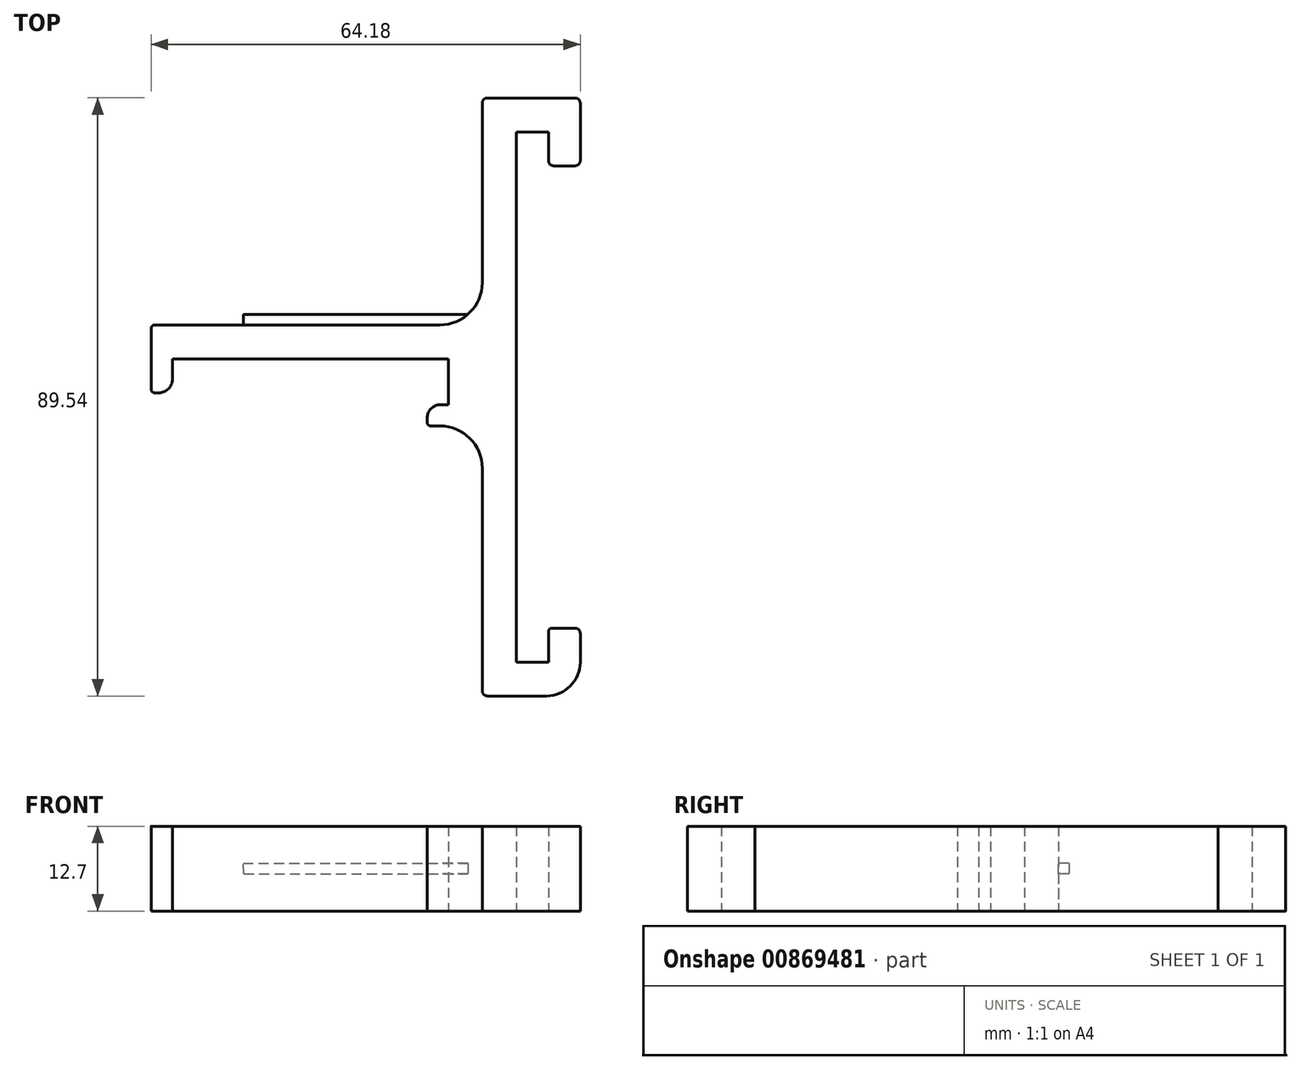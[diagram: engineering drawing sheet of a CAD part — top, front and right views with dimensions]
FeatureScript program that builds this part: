
annotation { "Feature Type Name" : "Feature", "Feature Type Description" : "" }
export const myFeature = defineFeature(function(context is Context, id is Id, definition is map)
    precondition{}
    {
        {
            var Q0;
            Q0=qCreatedBy(makeId("Top.planeOp"),FACE);
            var sketch = newSketch(context, id + "F0", { "sketchPlane" : qUnion([Q0])});
            skLineSegment(sketch, "E0", {"start": v(41.28, 0) * mm, "end": v(0, 0) * mm});
            skLineSegment(sketch, "E1", {"start": v(41.28, -6.86) * mm, "end": v(40.13, -6.86) * mm});
            skLineSegment(sketch, "E2", {"start": v(38.1, -8.89) * mm, "end": v(38.1, -9.53) * mm});
            skLineSegment(sketch, "E3", {"start": v(38.6, -10.03) * mm, "end": v(40, -10.03) * mm});
            skLineSegment(sketch, "E4", {"start": v(0, 0) * mm, "end": v(0, -3.05) * mm});
            skLineSegment(sketch, "E5.0", {"start": v(40, 5.08) * mm, "end": v(-2.67, 5.08) * mm});
            skLineSegment(sketch, "E6.0", {"start": v(-3.18, 4.57) * mm, "end": v(-3.18, -4.57) * mm});
            skLineSegment(sketch, "E7", {"start": v(-2.67, -5.08) * mm, "end": v(-2.03, -5.08) * mm});
            skLineSegment(sketch, "E8.0", {"start": v(55.92, -50.47) * mm, "end": v(47.1, -50.47) * mm});
            skLineSegment(sketch, "E9", {"start": v(46.34, -16.38) * mm, "end": v(46.34, -49.7) * mm});
            skLineSegment(sketch, "E10", {"start": v(46.34, 11.43) * mm, "end": v(46.34, 38.3) * mm});
            skLineSegment(sketch, "E11.0", {"start": v(51.42, 33.99) * mm, "end": v(51.42, -45.39) * mm});
            skLineSegment(sketch, "E12.0", {"start": v(56.25, 33.99) * mm, "end": v(56.25, 29.67) * mm});
            skLineSegment(sketch, "E13.0", {"start": v(56.25, -45.39) * mm, "end": v(51.42, -45.39) * mm});
            skLineSegment(sketch, "E14.0", {"start": v(61, -41.07) * mm, "end": v(61, -45.39) * mm});
            skLineSegment(sketch, "E15.0", {"start": v(56.25, 33.99) * mm, "end": v(51.42, 33.99) * mm});
            skLineSegment(sketch, "E16.0", {"start": v(60.24, 39.07) * mm, "end": v(47.1, 39.07) * mm});
            skLineSegment(sketch, "E17.0", {"start": v(60.24, -40.3) * mm, "end": v(56.76, -40.3) * mm});
            skLineSegment(sketch, "E18", {"start": v(56.25, -40.82) * mm, "end": v(56.25, -45.39) * mm});
            skLineSegment(sketch, "E19.0", {"start": v(60.24, 28.9) * mm, "end": v(57.01, 28.9) * mm});
            skLineSegment(sketch, "E20", {"start": v(61, 38.3) * mm, "end": v(61, 29.67) * mm});
            skLineSegment(sketch, "E21", {"start": v(41.28, 0) * mm, "end": v(41.28, -6.86) * mm});
            skPoint(sketch, "E22.visualSharp", {"position": v(61, -50.47) * mm});
            skArc(sketch, "E22.filletArc", {"start": v(55.92, -50.47) * mm, "mid": v(59.51, -48.98) * mm, "end": v(61, -45.39) * mm});
            skArc(sketch, "E23.filletArc", {"start": v(46.34, -49.7) * mm, "mid": v(46.57, -50.25) * mm, "end": v(47.1, -50.47) * mm});
            skPoint(sketch, "E24.visualSharp", {"position": v(61, -40.3) * mm});
            skArc(sketch, "E24.filletArc", {"start": v(61, -41.07) * mm, "mid": v(60.77, -40.53) * mm, "end": v(60.24, -40.3) * mm});
            skPoint(sketch, "E25.visualSharp", {"position": v(56.25, -40.3) * mm});
            skArc(sketch, "E25.filletArc", {"start": v(56.76, -40.3) * mm, "mid": v(56.4, -40.46) * mm, "end": v(56.25, -40.82) * mm});
            skPoint(sketch, "E26.visualSharp", {"position": v(56.25, 28.9) * mm});
            skArc(sketch, "E26.filletArc", {"start": v(56.25, 29.67) * mm, "mid": v(56.47, 29.13) * mm, "end": v(57.01, 28.9) * mm});
            skPoint(sketch, "E27.visualSharp", {"position": v(61, 28.9) * mm});
            skArc(sketch, "E27.filletArc", {"start": v(60.24, 28.9) * mm, "mid": v(60.77, 29.13) * mm, "end": v(61, 29.67) * mm});
            skPoint(sketch, "E28.visualSharp", {"position": v(61, 39.07) * mm});
            skArc(sketch, "E28.filletArc", {"start": v(61, 38.3) * mm, "mid": v(60.77, 38.84) * mm, "end": v(60.24, 39.07) * mm});
            skPoint(sketch, "E29.visualSharp", {"position": v(46.34, 39.07) * mm});
            skArc(sketch, "E29.filletArc", {"start": v(47.1, 39.07) * mm, "mid": v(46.57, 38.84) * mm, "end": v(46.34, 38.3) * mm});
            skPoint(sketch, "E30.visualSharp", {"position": v(46.34, 5.08) * mm});
            skArc(sketch, "E30.filletArc", {"start": v(40, 5.08) * mm, "mid": v(44.48, 6.94) * mm, "end": v(46.34, 11.43) * mm});
            skPoint(sketch, "E31.visualSharp", {"position": v(46.34, -10.03) * mm});
            skArc(sketch, "E31.filletArc", {"start": v(46.34, -16.38) * mm, "mid": v(44.48, -11.9) * mm, "end": v(40, -10.03) * mm});
            skPoint(sketch, "E32.visualSharp", {"position": v(-3.18, 5.08) * mm});
            skArc(sketch, "E32.filletArc", {"start": v(-2.67, 5.08) * mm, "mid": v(-3.03, 4.93) * mm, "end": v(-3.18, 4.57) * mm});
            skPoint(sketch, "E33.visualSharp", {"position": v(-3.18, -5.08) * mm});
            skArc(sketch, "E33.filletArc", {"start": v(-3.18, -4.57) * mm, "mid": v(-3.03, -4.93) * mm, "end": v(-2.67, -5.08) * mm});
            skPoint(sketch, "E34.visualSharp", {"position": v(38.1, -10.03) * mm});
            skArc(sketch, "E34.filletArc", {"start": v(38.1, -9.53) * mm, "mid": v(38.25, -9.88) * mm, "end": v(38.6, -10.03) * mm});
            skPoint(sketch, "E35.visualSharp", {"position": v(0, -5.08) * mm});
            skArc(sketch, "E35.filletArc", {"start": v(-2.03, -5.08) * mm, "mid": v(-0.6, -4.48) * mm, "end": v(0, -3.05) * mm});
            skPoint(sketch, "E36.visualSharp", {"position": v(38.1, -6.86) * mm});
            skArc(sketch, "E36.filletArc", {"start": v(40.13, -6.86) * mm, "mid": v(38.7, -7.45) * mm, "end": v(38.1, -8.89) * mm});
            skSolve(sketch);
        }
        {
            var Q0;
            Q0 = qSketchRegion(id + "F0", true);
            extrude(context, id + "F1", {"entities" : qUnion([Q0]), "depth" : 12.7 * mm, "offsetDistance" : 25.4 * mm});
        }
        {
            var Q0;
            Q0=makeQuery(id+"F1.opExtrude","SWEPT_FACE",FACE,{"disambiguationData":[OSD([sQuery(id+"F0.wireOp",EDGE,"E5.0")])]});
            cPlane(context, id + "F2", {"entities" : qUnion([Q0]), "cplaneType" : CPlaneType.OFFSET, "offset" : 0 * mm, "width" : 152.4 * mm, "height" : 152.4 * mm});
        }
        {
            var Q0;
            Q0=qCreatedBy(id+"F2.planeOp",FACE);
            var sketch = newSketch(context, id + "F3", { "sketchPlane" : qUnion([Q0])});
            skLineSegment(sketch, "E37", {"start": v(0, 19.25) * mm, "end": v(0, 0) * mm});
            skLineSegment(sketch, "E38", {"start": v(9.05, 0) * mm, "end": v(-27.4, 0) * mm});
            skLineSegment(sketch, "E39.0", {"start": v(-10.58, 7.14) * mm, "end": v(-46.34, 7.14) * mm});
            skLineSegment(sketch, "E40.0", {"start": v(-46.34, -6.35) * mm, "end": v(9.02, -6.35) * mm});
            skLineSegment(sketch, "E40.1", {"start": v(-46.34, 7.14) * mm, "end": v(-46.34, 5.56) * mm});
            skLineSegment(sketch, "E40.2", {"start": v(9.02, 19.05) * mm, "end": v(-46.34, 19.05) * mm});
            skLineSegment(sketch, "E41.0", {"start": v(-10.68, 5.56) * mm, "end": v(-46.34, 5.56) * mm});
            skLineSegment(sketch, "E42", {"start": v(-10.68, 5.56) * mm, "end": v(-10.58, 7.14) * mm});
            skSolve(sketch);
        }
        {
            var Q0;
            {var subQ5=sQuery(id+"F3.wireOp",EDGE,"E40.1");Q0=makeQuery(id+"F3.imprint","IMPRINT",FACE,{"disambiguationData":[TD([[makeQuery(id+"F3.imprint","IMPRINT",EDGE,{"derivedFrom":subQ5}),1.0]])]});}
            extrude(context, id + "F4", {"entities" : qUnion([Q0]), "operationType" : NewBodyOperationType.ADD, "depth" : 1.59 * mm, "offsetDistance" : 25.4 * mm});
        }
    });
